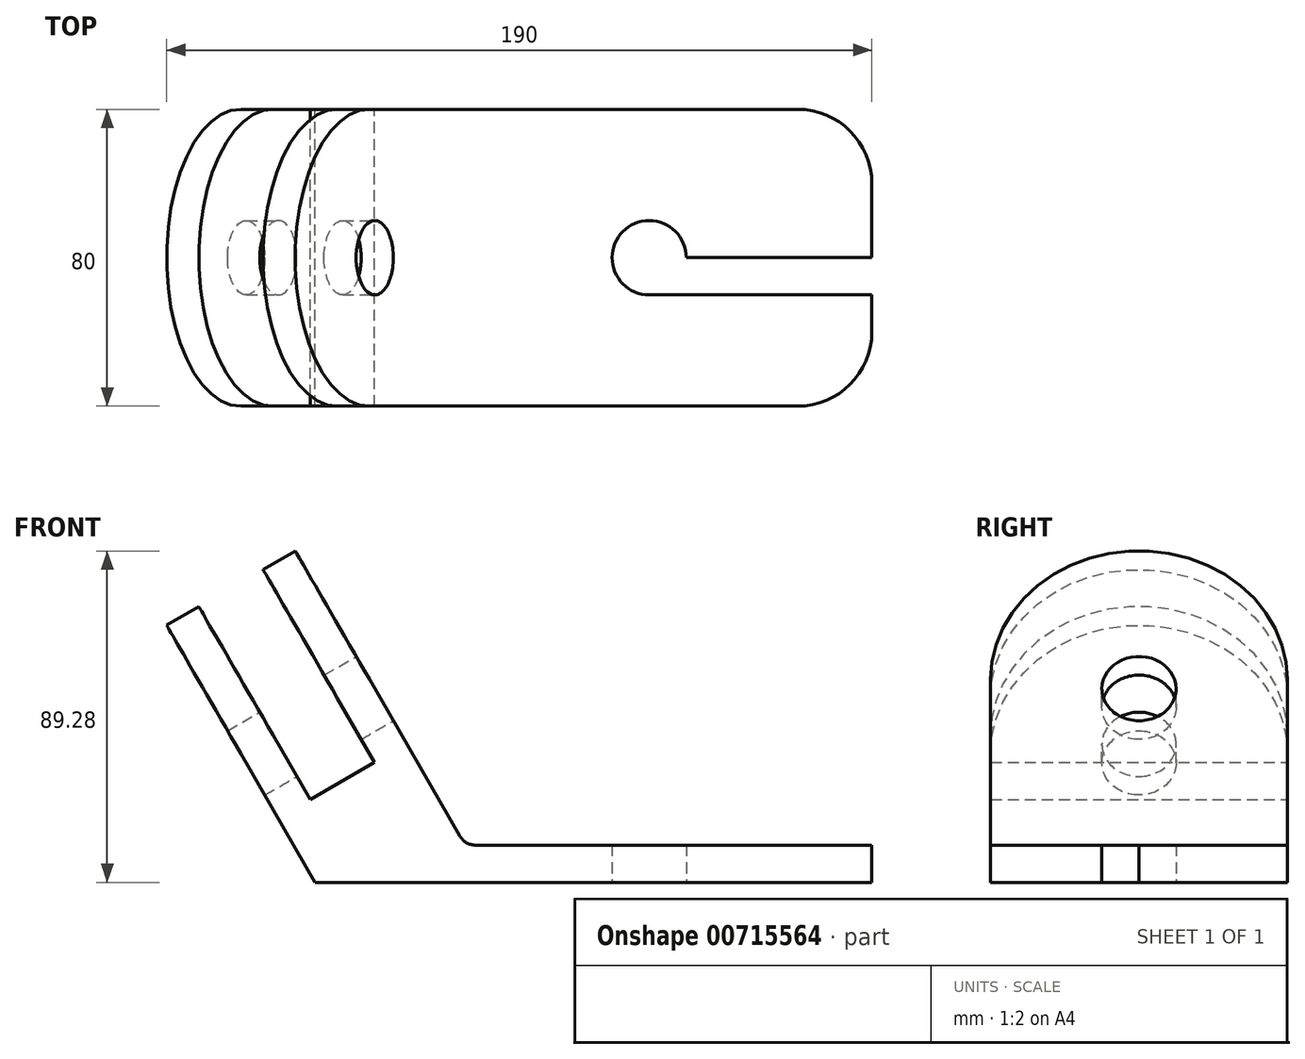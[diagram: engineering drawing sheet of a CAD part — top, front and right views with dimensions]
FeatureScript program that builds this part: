
annotation { "Feature Type Name" : "Feature", "Feature Type Description" : "" }
export const myFeature = defineFeature(function(context is Context, id is Id, definition is map)
    precondition{}
    {
        {
            var Q0;
            Q0=qCreatedBy(makeId("Front.planeOp"),FACE);
            var sketch = newSketch(context, id + "F0", { "sketchPlane" : qUnion([Q0])});
            skLineSegment(sketch, "E0", {"start": v(0, 0) * mm, "end": v(-150, 0) * mm});
            skLineSegment(sketch, "E1", {"start": v(0, 0) * mm, "end": v(0, 10) * mm});
            skLineSegment(sketch, "E2", {"start": v(-150, 0) * mm, "end": v(-190, 69.28) * mm});
            skLineSegment(sketch, "E3", {"start": v(-190, 69.28) * mm, "end": v(-181.34, 74.28) * mm});
            skLineSegment(sketch, "E4", {"start": v(-181.34, 74.28) * mm, "end": v(-151.34, 22.32) * mm});
            skLineSegment(sketch, "E5", {"start": v(-151.34, 22.32) * mm, "end": v(-134.02, 32.32) * mm});
            skLineSegment(sketch, "E6", {"start": v(-134.02, 32.32) * mm, "end": v(-164.02, 84.28) * mm});
            skLineSegment(sketch, "E7", {"start": v(-164.02, 84.28) * mm, "end": v(-155.36, 89.28) * mm});
            skLineSegment(sketch, "E8", {"start": v(0, 10) * mm, "end": v(-109.59, 10) * mm});
            skLineSegment(sketch, "E9", {"start": v(-155.36, 89.28) * mm, "end": v(-109.59, 10) * mm});
            skSolve(sketch);
        }
        {
            var Q0;
            Q0=makeQuery(id+"F0.imprint","IMPRINT",FACE,{"disambiguationData":[TD([[makeQuery(id+"F0.imprint","IMPRINT",EDGE,{"derivedFrom":sQuery(id+"F0.wireOp",EDGE,"E0")}),-1.0]])]});
            extrude(context, id + "F1", {"entities" : qUnion([Q0]), "depth" : 80 * mm, "offsetDistance" : 25 * mm});
        }
        {
            var Q0;
            Q0=qCreatedBy(makeId("Top.planeOp"),FACE);
            var sketch = newSketch(context, id + "F2", { "sketchPlane" : qUnion([Q0])});
            skLineSegment(sketch, "E10", {"start": v(0, 0) * mm, "end": v(0, -40) * mm});
            skLineSegment(sketch, "E11", {"start": v(0, -40) * mm, "end": v(-60, -40) * mm});
            skCircle(sketch, "E12", {"center": v(-60, -40) * mm, "radius": 10 * mm});
            skLineSegment(sketch, "E13", {"start": v(0, -40) * mm, "end": v(0, -30) * mm});
            skLineSegment(sketch, "E14", {"start": v(0, -30) * mm, "end": v(-60, -30) * mm});
            skLineSegment(sketch, "E15", {"start": v(-60, -30) * mm, "end": v(-60, -50) * mm});
            skLineSegment(sketch, "E16", {"start": v(-60, -50) * mm, "end": v(0, -50) * mm});
            skLineSegment(sketch, "E17", {"start": v(0, -50) * mm, "end": v(0, -40) * mm});
            skSolve(sketch);
        }
        {
            var Q0;
            {var subQ0=sQuery(id+"F2.wireOp",EDGE,"E15");var subQ4=makeQuery(id+"F2.imprint","INTERSECT",VERTEX,{"derivedFrom":[sQuery(id+"F2.wireOp",EDGE,"E11"),subQ0]});Q0=makeQuery(id+"F2.imprint","IMPRINT",FACE,{"disambiguationData":[TD([[makeQuery(id+"F2.imprint","IMPRINT",EDGE,{"disambiguationData":[TD([[subQ4,1.0]])],"derivedFrom":subQ0}),-1.0]])]});}
            var Q1;
            {var subQ0=sQuery(id+"F2.wireOp",EDGE,"E15");var subQ1=sQuery(id+"F2.wireOp",EDGE,"E11");var subQ2=makeQuery(id+"F2.imprint","INTERSECT",VERTEX,{"derivedFrom":[subQ1,subQ0]});Q1=makeQuery(id+"F2.imprint","IMPRINT",FACE,{"disambiguationData":[TD([[makeQuery(id+"F2.imprint","IMPRINT",EDGE,{"disambiguationData":[TD([[subQ2,1.0]])],"derivedFrom":subQ1}),-1.0]])]});}
            var Q2;
            {var subQ0=sQuery(id+"F2.wireOp",EDGE,"E15");var subQ1=sQuery(id+"F2.wireOp",EDGE,"E11");var subQ2=makeQuery(id+"F2.imprint","INTERSECT",VERTEX,{"derivedFrom":[subQ1,subQ0]});Q2=makeQuery(id+"F2.imprint","IMPRINT",FACE,{"disambiguationData":[TD([[makeQuery(id+"F2.imprint","IMPRINT",EDGE,{"disambiguationData":[TD([[subQ2,1.0]])],"derivedFrom":subQ1}),1.0]])]});}
            var Q3;
            {var subQ4=sQuery(id+"F2.wireOp",EDGE,"E16");Q3=makeQuery(id+"F2.imprint","IMPRINT",FACE,{"disambiguationData":[TD([[makeQuery(id+"F2.imprint","IMPRINT",EDGE,{"derivedFrom":subQ4}),1.0]])]});}
            var Q4;
            {var subQ0=sQuery(id+"F2.wireOp",EDGE,"E13");Q4=makeQuery(id+"F2.imprint","IMPRINT",FACE,{"disambiguationData":[TD([[makeQuery(id+"F2.imprint","IMPRINT",EDGE,{"derivedFrom":subQ0}),1.0]])]});}
            extrude(context, id + "F3", {"entities" : qUnion([Q0, Q1, Q2, Q3, Q4]), "operationType" : NewBodyOperationType.REMOVE, "depth" : 27.9 * mm, "offsetDistance" : 25 * mm});
        }
        {
            var Q0;
            Q0=makeQuery(id+"F1.opExtrude","CAP_EDGE",EDGE,{"disambiguationData":[OSD([sQuery(id+"F0.wireOp",EDGE,"E1")])],"isStart":true});
            var Q1;
            Q1=makeQuery(id+"F1.opExtrude","CAP_EDGE",EDGE,{"disambiguationData":[OSD([sQuery(id+"F0.wireOp",EDGE,"E1")])],"isStart":false});
            fillet(context, id + "F4", {"entities" : qUnion([Q0, Q1]), "radius" : 20 * mm, "tangentPropagation" : true, "allowEdgeOverflow" : false});
        }
        {
            var Q0;
            Q0=makeQuery(id+"F1.opExtrude","SWEPT_FACE",FACE,{"disambiguationData":[OSD([sQuery(id+"F0.wireOp",EDGE,"E9")])]});
            var sketch = newSketch(context, id + "F5", { "sketchPlane" : qUnion([Q0])});
            skLineSegment(sketch, "E18", {"start": v(-40, 63.45) * mm, "end": v(-40, 112.15) * mm});
            skLineSegment(sketch, "E19", {"start": v(-40, 112.15) * mm, "end": v(-80, 112.15) * mm});
            skPoint(sketch, "E19.endSnap0", {"position": v(-80, 109.23) * mm});
            skCircle(sketch, "E20", {"center": v(-40, 112.15) * mm, "radius": 10 * mm});
            skSolve(sketch);
        }
        {
            var Q0;
            Q0=makeQuery(id+"F1.opExtrude","CAP_EDGE",EDGE,{"disambiguationData":[OSD([sQuery(id+"F0.wireOp",EDGE,"E7")])],"isStart":true});
            var Q1;
            Q1=makeQuery(id+"F1.opExtrude","CAP_EDGE",EDGE,{"disambiguationData":[OSD([sQuery(id+"F0.wireOp",EDGE,"E3")])],"isStart":true});
            var Q2;
            Q2=makeQuery(id+"F1.opExtrude","CAP_EDGE",EDGE,{"disambiguationData":[OSD([sQuery(id+"F0.wireOp",EDGE,"E3")])],"isStart":false});
            var Q3;
            Q3=makeQuery(id+"F1.opExtrude","CAP_EDGE",EDGE,{"disambiguationData":[OSD([sQuery(id+"F0.wireOp",EDGE,"E7")])],"isStart":false});
            fillet(context, id + "F6", {"entities" : qUnion([Q0, Q1, Q2, Q3]), "radius" : 40 * mm, "tangentPropagation" : true, "allowEdgeOverflow" : false});
        }
        {
            var Q0;
            Q0=makeQuery(id+"F1.opExtrude","SWEPT_EDGE",EDGE,{"disambiguationData":[OSD([sQuery(id+"F0.wireOp",EDGE,"E8"),sQuery(id+"F0.wireOp",EDGE,"E9")])]});
            fillet(context, id + "F7", {"entities" : qUnion([Q0]), "radius" : 5 * mm, "tangentPropagation" : true, "allowEdgeOverflow" : false});
        }
        {
            var Q0;
            {var subQ0=sQuery(id+"F5.wireOp",EDGE,"E19");var subQ1=sQuery(id+"F5.wireOp",EDGE,"E18");var subQ2=makeQuery(id+"F5.imprint","INTERSECT",VERTEX,{"derivedFrom":[subQ1,subQ0]});Q0=makeQuery(id+"F5.imprint","IMPRINT",FACE,{"disambiguationData":[TD([[makeQuery(id+"F5.imprint","IMPRINT",EDGE,{"disambiguationData":[TD([[subQ2,1.0]])],"derivedFrom":subQ1}),-1.0]])]});}
            var Q1;
            {var subQ0=sQuery(id+"F5.wireOp",EDGE,"E19");var subQ1=sQuery(id+"F5.wireOp",EDGE,"E18");var subQ2=makeQuery(id+"F5.imprint","INTERSECT",VERTEX,{"derivedFrom":[subQ1,subQ0]});Q1=makeQuery(id+"F5.imprint","IMPRINT",FACE,{"disambiguationData":[TD([[makeQuery(id+"F5.imprint","IMPRINT",EDGE,{"disambiguationData":[TD([[subQ2,1.0]])],"derivedFrom":subQ1}),1.0]])]});}
            extrude(context, id + "F8", {"entities" : qUnion([Q0, Q1]), "operationType" : NewBodyOperationType.REMOVE, "oppositeDirection" : true, "depth" : 148.2 * mm, "offsetDistance" : 25 * mm});
        }
    });
